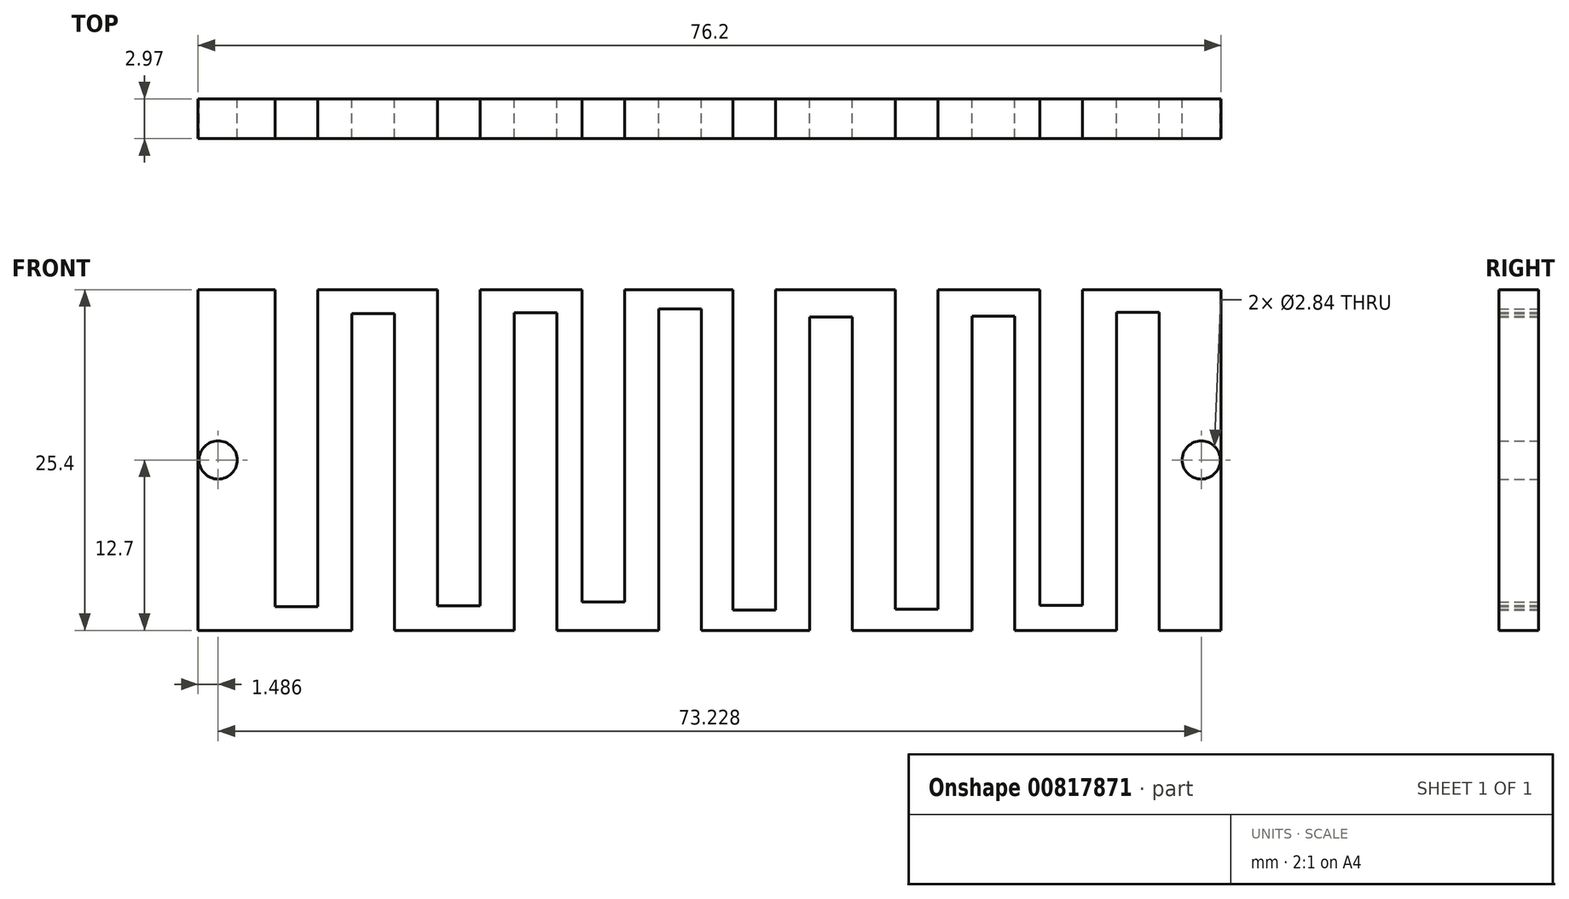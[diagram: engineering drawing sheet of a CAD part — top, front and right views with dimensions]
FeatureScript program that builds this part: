
annotation { "Feature Type Name" : "Feature", "Feature Type Description" : "" }
export const myFeature = defineFeature(function(context is Context, id is Id, definition is map)
    precondition{}
    {
        {
            var Q0;
            Q0=qCreatedBy(makeId("Front.planeOp"),FACE);
            var sketch = newSketch(context, id + "F0", { "sketchPlane" : qUnion([Q0])});
            skLineSegment(sketch, "E0.bottom", {"start": v(0, 0) * mm, "end": v(-76.2, 0) * mm});
            skLineSegment(sketch, "E0.top", {"start": v(0, 25.4) * mm, "end": v(-76.2, 25.4) * mm});
            skLineSegment(sketch, "E0.left", {"start": v(0, 0) * mm, "end": v(0, 25.4) * mm});
            skLineSegment(sketch, "E0.right", {"start": v(-76.2, 0) * mm, "end": v(-76.2, 25.4) * mm});
            skLineSegment(sketch, "E1.bottom", {"start": v(-70.48, 25.9) * mm, "end": v(-67.3, 25.9) * mm});
            skLineSegment(sketch, "E1.top", {"start": v(-70.48, 1.78) * mm, "end": v(-67.3, 1.78) * mm});
            skLineSegment(sketch, "E1.left", {"start": v(-70.48, 25.9) * mm, "end": v(-70.48, 1.78) * mm});
            skLineSegment(sketch, "E1.right", {"start": v(-67.3, 25.9) * mm, "end": v(-67.3, 1.78) * mm});
            skCircle(sketch, "E2", {"center": v(-74.71, 12.7) * mm, "radius": 1.42 * mm});
            skCircle(sketch, "E3", {"center": v(-1.49, 12.7) * mm, "radius": 1.42 * mm});
            skLineSegment(sketch, "E4.bottom", {"start": v(-64.76, 23.62) * mm, "end": v(-61.59, 23.62) * mm});
            skLineSegment(sketch, "E4.top", {"start": v(-64.76, -0.5) * mm, "end": v(-61.59, -0.5) * mm});
            skLineSegment(sketch, "E4.left", {"start": v(-64.76, 23.62) * mm, "end": v(-64.76, -0.5) * mm});
            skLineSegment(sketch, "E4.right", {"start": v(-61.59, 23.62) * mm, "end": v(-61.59, -0.5) * mm});
            skLineSegment(sketch, "E5.bottom", {"start": v(-58.37, 25.96) * mm, "end": v(-55.2, 25.96) * mm});
            skLineSegment(sketch, "E5.top", {"start": v(-58.37, 1.83) * mm, "end": v(-55.2, 1.83) * mm});
            skLineSegment(sketch, "E5.left", {"start": v(-58.37, 25.96) * mm, "end": v(-58.37, 1.83) * mm});
            skLineSegment(sketch, "E5.right", {"start": v(-55.2, 25.96) * mm, "end": v(-55.2, 1.83) * mm});
            skLineSegment(sketch, "E6.bottom", {"start": v(-52.66, 23.68) * mm, "end": v(-49.48, 23.68) * mm});
            skLineSegment(sketch, "E6.top", {"start": v(-52.66, -0.45) * mm, "end": v(-49.48, -0.45) * mm});
            skLineSegment(sketch, "E6.left", {"start": v(-52.66, 23.68) * mm, "end": v(-52.66, -0.45) * mm});
            skLineSegment(sketch, "E6.right", {"start": v(-49.48, 23.68) * mm, "end": v(-49.48, -0.45) * mm});
            skLineSegment(sketch, "E7.bottom", {"start": v(-47.62, 26.23) * mm, "end": v(-44.44, 26.23) * mm});
            skLineSegment(sketch, "E7.top", {"start": v(-47.62, 2.1) * mm, "end": v(-44.44, 2.1) * mm});
            skLineSegment(sketch, "E7.left", {"start": v(-47.62, 26.23) * mm, "end": v(-47.62, 2.1) * mm});
            skLineSegment(sketch, "E7.right", {"start": v(-44.44, 26.23) * mm, "end": v(-44.44, 2.1) * mm});
            skLineSegment(sketch, "E8.bottom", {"start": v(-41.9, 23.95) * mm, "end": v(-38.73, 23.95) * mm});
            skLineSegment(sketch, "E8.top", {"start": v(-41.9, -0.18) * mm, "end": v(-38.73, -0.18) * mm});
            skLineSegment(sketch, "E8.left", {"start": v(-41.9, 23.95) * mm, "end": v(-41.9, -0.18) * mm});
            skLineSegment(sketch, "E8.right", {"start": v(-38.73, 23.95) * mm, "end": v(-38.73, -0.18) * mm});
            skLineSegment(sketch, "E9.bottom", {"start": v(-36.38, 25.66) * mm, "end": v(-33.2, 25.66) * mm});
            skLineSegment(sketch, "E9.top", {"start": v(-36.38, 1.53) * mm, "end": v(-33.2, 1.53) * mm});
            skLineSegment(sketch, "E9.left", {"start": v(-36.38, 25.66) * mm, "end": v(-36.38, 1.53) * mm});
            skLineSegment(sketch, "E9.right", {"start": v(-33.2, 25.66) * mm, "end": v(-33.2, 1.53) * mm});
            skLineSegment(sketch, "E10.bottom", {"start": v(-30.66, 23.37) * mm, "end": v(-27.49, 23.37) * mm});
            skLineSegment(sketch, "E10.top", {"start": v(-30.66, -0.76) * mm, "end": v(-27.49, -0.76) * mm});
            skLineSegment(sketch, "E10.left", {"start": v(-30.66, 23.37) * mm, "end": v(-30.66, -0.76) * mm});
            skLineSegment(sketch, "E10.right", {"start": v(-27.49, 23.37) * mm, "end": v(-27.49, -0.76) * mm});
            skLineSegment(sketch, "E11.bottom", {"start": v(-24.28, 25.71) * mm, "end": v(-21.1, 25.71) * mm});
            skLineSegment(sketch, "E11.top", {"start": v(-24.28, 1.58) * mm, "end": v(-21.1, 1.58) * mm});
            skLineSegment(sketch, "E11.left", {"start": v(-24.28, 25.71) * mm, "end": v(-24.28, 1.58) * mm});
            skLineSegment(sketch, "E11.right", {"start": v(-21.1, 25.71) * mm, "end": v(-21.1, 1.58) * mm});
            skLineSegment(sketch, "E12.bottom", {"start": v(-18.56, 23.42) * mm, "end": v(-15.39, 23.42) * mm});
            skLineSegment(sketch, "E12.top", {"start": v(-18.56, -0.7) * mm, "end": v(-15.39, -0.7) * mm});
            skLineSegment(sketch, "E12.left", {"start": v(-18.56, 23.42) * mm, "end": v(-18.56, -0.7) * mm});
            skLineSegment(sketch, "E12.right", {"start": v(-15.39, 23.42) * mm, "end": v(-15.39, -0.7) * mm});
            skLineSegment(sketch, "E13.bottom", {"start": v(-13.52, 25.98) * mm, "end": v(-10.34, 25.98) * mm});
            skLineSegment(sketch, "E13.top", {"start": v(-13.52, 1.85) * mm, "end": v(-10.34, 1.85) * mm});
            skLineSegment(sketch, "E13.left", {"start": v(-13.52, 25.98) * mm, "end": v(-13.52, 1.85) * mm});
            skLineSegment(sketch, "E13.right", {"start": v(-10.34, 25.98) * mm, "end": v(-10.34, 1.85) * mm});
            skLineSegment(sketch, "E14.bottom", {"start": v(-7.8, 23.7) * mm, "end": v(-4.63, 23.7) * mm});
            skLineSegment(sketch, "E14.top", {"start": v(-7.8, -0.43) * mm, "end": v(-4.63, -0.43) * mm});
            skLineSegment(sketch, "E14.left", {"start": v(-7.8, 23.7) * mm, "end": v(-7.8, -0.43) * mm});
            skLineSegment(sketch, "E14.right", {"start": v(-4.63, 23.7) * mm, "end": v(-4.63, -0.43) * mm});
            skSolve(sketch);
        }
        {
            var Q0;
            Q0=makeQuery(id+"F0.imprint","IMPRINT",FACE,{"disambiguationData":[TD([[makeQuery(id+"F0.imprint","IMPRINT",EDGE,{"derivedFrom":sQuery(id+"F0.wireOp",EDGE,"E0.bottom")}),-1.0]])]});
            extrude(context, id + "F1", {"entities" : qUnion([Q0]), "depth" : 2.97 * mm, "offsetDistance" : 25.4 * mm});
        }
    });
